# Revit family: Elite_XXXX_Standard
name_source: partatom
category: Windows
revit_build: Autodesk Revit 2014 (Build: 20130308_1515(x64)
units: mm (PartAtom-declared; Revit-internal decimal feet)

## types (42) — shared parameters
Astragal Sash Gap = 1 mm  [stored 0.00328084 ft]
Centered In Wall = Yes
Custom Sash Width Side = 800 mm  [stored 2.62467 ft]
Default Sill Height = 800 mm  [stored 2.62467 ft]
Description = Elite Slideing Window XXXX
Equal Sash Width = Yes
Frame Thickness = 70 mm
Glass Type = Glass
Glazing Thickness = 4 mm  [stored 0.0131234 ft]
Limit Sash Height Max = 1800 mm  [stored 5.90551 ft]
Limit Sash Height Min = 300 mm  [stored 0.984252 ft]
Limit Sash Width Max = 1500 mm  [stored 4.92126 ft]
Limit Sash Width Min = 300 mm  [stored 0.984252 ft]
Limit Sash Width Side Min = 300 mm  [stored 0.984252 ft]
Limit Window Height Min = 383 mm  [stored 1.25656 ft]
Limit Window Width Min = 1167 mm
Manufacturer = Crealco
Model = Elite Slideing Window XXXX
Sash Frame Seal = 1 mm  [stored 0.00328084 ft]
Sash Rail Fore Aft Spacing = 5 mm  [stored 0.0164042 ft]
Sash Side Spacing = 1 mm  [stored 0.00328084 ft]
Wall Closure = By host
zero-valued in all types: Custom Frame Offset From Exterior

## per-type parameters (varying)
| type | Area Middle Sash Glazing | Area Side Sash Glazing | Custom Windload | Custom Window Height | Custom Window Width | Height | Inside Heavy Duty Interlocker | Interlocker Configuration | Limit Sash Width Side Max | Limit Window Height Max | Limit Window Width Max | Max Pane Area | Outside Heavy Duty Interlocker | Sash Height | Sash Width Middle | Sash Width Sides | Width | Windload Design |
| XXXX_Custom | 0.23 m² | 0.23 m² | 1000 mm  [stored 3.28084 ft] | 590 mm  [stored 1.9357 ft] | 2390 mm  [stored 7.84121 ft] | 590 mm  [stored 1.9357 ft] | No | 0 mm  [stored 0 ft] | 912 mm | 1883 mm | 2990 mm  [stored 9.80971 ft] | 0.23 m² | No | 507 mm | 606 mm | 606 mm | 2390 mm  [stored 7.84121 ft] | 1000 mm  [stored 3.28084 ft] |
| Elite-2406XXXX-1000Pa | 0.23 m² | 0.23 m² | 1000 mm  [stored 3.28084 ft] | 590 mm  [stored 1.9357 ft] | 2390 mm  [stored 7.84121 ft] | 590 mm  [stored 1.9357 ft] | No | 0 mm  [stored 0 ft] | 912 mm | 1883 mm | 2990 mm  [stored 9.80971 ft] | 0.23 m² | No | 507 mm | 606 mm | 606 mm | 2390 mm  [stored 7.84121 ft] | 1000 mm  [stored 3.28084 ft] |
| Elite-2406XXXX-1500Pa | 0.23 m² | 0.23 m² | 1500 mm  [stored 4.92126 ft] | 590 mm  [stored 1.9357 ft] | 2390 mm  [stored 7.84121 ft] | 590 mm  [stored 1.9357 ft] | No | 0 mm  [stored 0 ft] | 912 mm | 1883 mm | 2990 mm  [stored 9.80971 ft] | 0.23 m² | No | 507 mm | 606 mm | 606 mm | 2390 mm  [stored 7.84121 ft] | 1500 mm  [stored 4.92126 ft] |
| Elite-2406XXXX-2000Pa | 0.23 m² | 0.23 m² | 2000 mm  [stored 6.56168 ft] | 590 mm  [stored 1.9357 ft] | 2390 mm  [stored 7.84121 ft] | 590 mm  [stored 1.9357 ft] | No | 0 mm  [stored 0 ft] | 912 mm | 1490 mm  [stored 4.88845 ft] | 2990 mm  [stored 9.80971 ft] | 0.23 m² | No | 507 mm | 606 mm | 606 mm | 2390 mm  [stored 7.84121 ft] | 2000 mm  [stored 6.56168 ft] |
| Elite-2706XXXX-1000Pa | 0.26 m² | 0.26 m² | 1000 mm  [stored 3.28084 ft] | 590 mm  [stored 1.9357 ft] | 2690 mm | 590 mm  [stored 1.9357 ft] | No | 0 mm  [stored 0 ft] | 1062 mm | 1883 mm | 2990 mm  [stored 9.80971 ft] | 0.26 m² | No | 507 mm | 681 mm | 681 mm | 2690 mm | 1000 mm  [stored 3.28084 ft] |
| Elite-2706XXXX-1500Pa | 0.26 m² | 0.26 m² | 1500 mm  [stored 4.92126 ft] | 590 mm  [stored 1.9357 ft] | 2690 mm | 590 mm  [stored 1.9357 ft] | No | 0 mm  [stored 0 ft] | 1062 mm | 1883 mm | 2990 mm  [stored 9.80971 ft] | 0.26 m² | No | 507 mm | 681 mm | 681 mm | 2690 mm | 1500 mm  [stored 4.92126 ft] |
| Elite-2706XXXX-2000Pa | 0.26 m² | 0.26 m² | 2000 mm  [stored 6.56168 ft] | 590 mm  [stored 1.9357 ft] | 2690 mm | 590 mm  [stored 1.9357 ft] | No | 0 mm  [stored 0 ft] | 1062 mm | 1490 mm  [stored 4.88845 ft] | 2990 mm  [stored 9.80971 ft] | 0.26 m² | No | 507 mm | 681 mm | 681 mm | 2690 mm | 2000 mm  [stored 6.56168 ft] |
| Elite-3006XXXX-1000Pa | 0.29 m² | 0.29 m² | 1000 mm  [stored 3.28084 ft] | 590 mm  [stored 1.9357 ft] | 2990 mm  [stored 9.80971 ft] | 590 mm  [stored 1.9357 ft] | No | 0 mm  [stored 0 ft] | 1212 mm | 1883 mm | 2990 mm  [stored 9.80971 ft] | 0.29 m² | No | 507 mm | 756 mm | 756 mm | 2990 mm  [stored 9.80971 ft] | 1000 mm  [stored 3.28084 ft] |
| Elite-3006XXXX-1500Pa | 0.29 m² | 0.29 m² | 1500 mm  [stored 4.92126 ft] | 590 mm  [stored 1.9357 ft] | 2990 mm  [stored 9.80971 ft] | 590 mm  [stored 1.9357 ft] | No | 0 mm  [stored 0 ft] | 1212 mm | 1883 mm | 2990 mm  [stored 9.80971 ft] | 0.29 m² | No | 507 mm | 756 mm | 756 mm | 2990 mm  [stored 9.80971 ft] | 1500 mm  [stored 4.92126 ft] |
| Elite-3006XXXX-2000Pa | 0.29 m² | 0.29 m² | 2000 mm  [stored 6.56168 ft] | 590 mm  [stored 1.9357 ft] | 2990 mm  [stored 9.80971 ft] | 590 mm  [stored 1.9357 ft] | No | 0 mm  [stored 0 ft] | 1212 mm | 1490 mm  [stored 4.88845 ft] | 2990 mm  [stored 9.80971 ft] | 0.29 m² | No | 507 mm | 756 mm | 756 mm | 2990 mm  [stored 9.80971 ft] | 2000 mm  [stored 6.56168 ft] |
| Elite-2409XXXX-1000Pa | 0.39 m² | 0.39 m² | 1000 mm  [stored 3.28084 ft] | 890 mm  [stored 2.91995 ft] | 2390 mm  [stored 7.84121 ft] | 890 mm  [stored 2.91995 ft] | No | 0 mm  [stored 0 ft] | 912 mm | 1883 mm | 2990 mm  [stored 9.80971 ft] | 0.39 m² | No | 807 mm  [stored 2.64764 ft] | 606 mm | 606 mm | 2390 mm  [stored 7.84121 ft] | 1000 mm  [stored 3.28084 ft] |
| Elite-2409XXXX-1500Pa | 0.39 m² | 0.39 m² | 1500 mm  [stored 4.92126 ft] | 890 mm  [stored 2.91995 ft] | 2390 mm  [stored 7.84121 ft] | 890 mm  [stored 2.91995 ft] | No | 0 mm  [stored 0 ft] | 912 mm | 1883 mm | 2990 mm  [stored 9.80971 ft] | 0.39 m² | No | 807 mm  [stored 2.64764 ft] | 606 mm | 606 mm | 2390 mm  [stored 7.84121 ft] | 1500 mm  [stored 4.92126 ft] |
| Elite-2409XXXX-2000Pa | 0.39 m² | 0.39 m² | 2000 mm  [stored 6.56168 ft] | 890 mm  [stored 2.91995 ft] | 2390 mm  [stored 7.84121 ft] | 890 mm  [stored 2.91995 ft] | No | 0 mm  [stored 0 ft] | 912 mm | 1490 mm  [stored 4.88845 ft] | 2990 mm  [stored 9.80971 ft] | 0.39 m² | No | 807 mm  [stored 2.64764 ft] | 606 mm | 606 mm | 2390 mm  [stored 7.84121 ft] | 2000 mm  [stored 6.56168 ft] |
| Elite-2709XXXX-1000Pa | 0.44 m² | 0.44 m² | 1000 mm  [stored 3.28084 ft] | 890 mm  [stored 2.91995 ft] | 2690 mm | 890 mm  [stored 2.91995 ft] | No | 0 mm  [stored 0 ft] | 1062 mm | 1883 mm | 2990 mm  [stored 9.80971 ft] | 0.44 m² | No | 807 mm  [stored 2.64764 ft] | 681 mm | 681 mm | 2690 mm | 1000 mm  [stored 3.28084 ft] |
| Elite-2709XXXX-1500Pa | 0.44 m² | 0.44 m² | 1500 mm  [stored 4.92126 ft] | 890 mm  [stored 2.91995 ft] | 2690 mm | 890 mm  [stored 2.91995 ft] | No | 0 mm  [stored 0 ft] | 1062 mm | 1883 mm | 2990 mm  [stored 9.80971 ft] | 0.44 m² | No | 807 mm  [stored 2.64764 ft] | 681 mm | 681 mm | 2690 mm | 1500 mm  [stored 4.92126 ft] |
| Elite-2709XXXX-2000Pa | 0.44 m² | 0.44 m² | 2000 mm  [stored 6.56168 ft] | 890 mm  [stored 2.91995 ft] | 2690 mm | 890 mm  [stored 2.91995 ft] | No | 0 mm  [stored 0 ft] | 1062 mm | 1490 mm  [stored 4.88845 ft] | 2990 mm  [stored 9.80971 ft] | 0.44 m² | No | 807 mm  [stored 2.64764 ft] | 681 mm | 681 mm | 2690 mm | 2000 mm  [stored 6.56168 ft] |
| Elite-3009XXXX-1000Pa | 0.5 m² | 0.5 m² | 1000 mm  [stored 3.28084 ft] | 890 mm  [stored 2.91995 ft] | 2990 mm  [stored 9.80971 ft] | 890 mm  [stored 2.91995 ft] | No | 0 mm  [stored 0 ft] | 1212 mm | 1883 mm | 2990 mm  [stored 9.80971 ft] | 0.5 m² | No | 807 mm  [stored 2.64764 ft] | 756 mm | 756 mm | 2990 mm  [stored 9.80971 ft] | 1000 mm  [stored 3.28084 ft] |
| Elite-3009XXXX-1500Pa | 0.5 m² | 0.5 m² | 1500 mm  [stored 4.92126 ft] | 890 mm  [stored 2.91995 ft] | 2990 mm  [stored 9.80971 ft] | 890 mm  [stored 2.91995 ft] | No | 0 mm  [stored 0 ft] | 1212 mm | 1883 mm | 2990 mm  [stored 9.80971 ft] | 0.5 m² | No | 807 mm  [stored 2.64764 ft] | 756 mm | 756 mm | 2990 mm  [stored 9.80971 ft] | 1500 mm  [stored 4.92126 ft] |
| Elite-3009XXXX-2000Pa | 0.5 m² | 0.5 m² | 2000 mm  [stored 6.56168 ft] | 890 mm  [stored 2.91995 ft] | 2990 mm  [stored 9.80971 ft] | 890 mm  [stored 2.91995 ft] | No | 0 mm  [stored 0 ft] | 1212 mm | 1490 mm  [stored 4.88845 ft] | 2990 mm  [stored 9.80971 ft] | 0.5 m² | No | 807 mm  [stored 2.64764 ft] | 756 mm | 756 mm | 2990 mm  [stored 9.80971 ft] | 2000 mm  [stored 6.56168 ft] |
| Elite-2412XXXX-1000Pa | 0.55 m² | 0.55 m² | 1000 mm  [stored 3.28084 ft] | 1190 mm  [stored 3.9042 ft] | 2390 mm  [stored 7.84121 ft] | 1190 mm  [stored 3.9042 ft] | No | 0 mm  [stored 0 ft] | 912 mm | 1883 mm | 2990 mm  [stored 9.80971 ft] | 0.55 m² | No | 1107 mm  [stored 3.63189 ft] | 606 mm | 606 mm | 2390 mm  [stored 7.84121 ft] | 1000 mm  [stored 3.28084 ft] |
| Elite-2412XXXX-1500Pa | 0.55 m² | 0.55 m² | 1500 mm  [stored 4.92126 ft] | 1190 mm  [stored 3.9042 ft] | 2390 mm  [stored 7.84121 ft] | 1190 mm  [stored 3.9042 ft] | No | 0 mm  [stored 0 ft] | 912 mm | 1883 mm | 2990 mm  [stored 9.80971 ft] | 0.55 m² | No | 1107 mm  [stored 3.63189 ft] | 606 mm | 606 mm | 2390 mm  [stored 7.84121 ft] | 1500 mm  [stored 4.92126 ft] |
| Elite-2412XXXX-2000Pa | 0.55 m² | 0.55 m² | 2000 mm  [stored 6.56168 ft] | 1190 mm  [stored 3.9042 ft] | 2390 mm  [stored 7.84121 ft] | 1190 mm  [stored 3.9042 ft] | Yes | 1 mm  [stored 0.00328084 ft] | 912 mm | 1490 mm  [stored 4.88845 ft] | 2990 mm  [stored 9.80971 ft] | 0.55 m² | No | 1107 mm  [stored 3.63189 ft] | 606 mm | 606 mm | 2390 mm  [stored 7.84121 ft] | 2000 mm  [stored 6.56168 ft] |
| Elite-2712XXXX-1000Pa | 0.63 m² | 0.63 m² | 1000 mm  [stored 3.28084 ft] | 1190 mm  [stored 3.9042 ft] | 2690 mm | 1190 mm  [stored 3.9042 ft] | No | 0 mm  [stored 0 ft] | 1062 mm | 1883 mm | 2990 mm  [stored 9.80971 ft] | 0.63 m² | No | 1107 mm  [stored 3.63189 ft] | 681 mm | 681 mm | 2690 mm | 1000 mm  [stored 3.28084 ft] |
| Elite-2712XXXX-1500Pa | 0.63 m² | 0.63 m² | 1500 mm  [stored 4.92126 ft] | 1190 mm  [stored 3.9042 ft] | 2690 mm | 1190 mm  [stored 3.9042 ft] | No | 0 mm  [stored 0 ft] | 1062 mm | 1883 mm | 2990 mm  [stored 9.80971 ft] | 0.63 m² | No | 1107 mm  [stored 3.63189 ft] | 681 mm | 681 mm | 2690 mm | 1500 mm  [stored 4.92126 ft] |
| Elite-2712XXXX-2000Pa | 0.63 m² | 0.63 m² | 2000 mm  [stored 6.56168 ft] | 1190 mm  [stored 3.9042 ft] | 2690 mm | 1190 mm  [stored 3.9042 ft] | Yes | 1 mm  [stored 0.00328084 ft] | 1062 mm | 1490 mm  [stored 4.88845 ft] | 2990 mm  [stored 9.80971 ft] | 0.63 m² | No | 1107 mm  [stored 3.63189 ft] | 681 mm | 681 mm | 2690 mm | 2000 mm  [stored 6.56168 ft] |
| Elite-3012XXXX-1000Pa | 0.7 m² | 0.7 m² | 1000 mm  [stored 3.28084 ft] | 1190 mm  [stored 3.9042 ft] | 2990 mm  [stored 9.80971 ft] | 1190 mm  [stored 3.9042 ft] | No | 0 mm  [stored 0 ft] | 1212 mm | 1883 mm | 2990 mm  [stored 9.80971 ft] | 0.7 m² | No | 1107 mm  [stored 3.63189 ft] | 756 mm | 756 mm | 2990 mm  [stored 9.80971 ft] | 1000 mm  [stored 3.28084 ft] |
| Elite-3012XXXX-1500Pa | 0.7 m² | 0.7 m² | 1500 mm  [stored 4.92126 ft] | 1190 mm  [stored 3.9042 ft] | 2990 mm  [stored 9.80971 ft] | 1190 mm  [stored 3.9042 ft] | Yes | 1 mm  [stored 0.00328084 ft] | 1212 mm | 1883 mm | 2990 mm  [stored 9.80971 ft] | 0.7 m² | No | 1107 mm  [stored 3.63189 ft] | 756 mm | 756 mm | 2990 mm  [stored 9.80971 ft] | 1500 mm  [stored 4.92126 ft] |
| Elite-3012XXXX-2000Pa | 0.7 m² | 0.7 m² | 2000 mm  [stored 6.56168 ft] | 1190 mm  [stored 3.9042 ft] | 2990 mm  [stored 9.80971 ft] | 1190 mm  [stored 3.9042 ft] | Yes | 1 mm  [stored 0.00328084 ft] | 1212 mm | 1490 mm  [stored 4.88845 ft] | 2990 mm  [stored 9.80971 ft] | 0.7 m² | No | 1107 mm  [stored 3.63189 ft] | 756 mm | 756 mm | 2990 mm  [stored 9.80971 ft] | 2000 mm  [stored 6.56168 ft] |
| Elite-2415XXXX-1000Pa | 0.72 m² | 0.72 m² | 1000 mm  [stored 3.28084 ft] | 1490 mm  [stored 4.88845 ft] | 2390 mm  [stored 7.84121 ft] | 1490 mm  [stored 4.88845 ft] | Yes | 1 mm  [stored 0.00328084 ft] | 912 mm | 1883 mm | 2990 mm  [stored 9.80971 ft] | 0.72 m² | No | 1407 mm  [stored 4.61614 ft] | 606 mm | 606 mm | 2390 mm  [stored 7.84121 ft] | 1000 mm  [stored 3.28084 ft] |
| Elite-2415XXXX-1500Pa | 0.72 m² | 0.72 m² | 1500 mm  [stored 4.92126 ft] | 1490 mm  [stored 4.88845 ft] | 2390 mm  [stored 7.84121 ft] | 1490 mm  [stored 4.88845 ft] | Yes | 1 mm  [stored 0.00328084 ft] | 912 mm | 1883 mm | 2990 mm  [stored 9.80971 ft] | 0.72 m² | No | 1407 mm  [stored 4.61614 ft] | 606 mm | 606 mm | 2390 mm  [stored 7.84121 ft] | 1500 mm  [stored 4.92126 ft] |
| Elite-2415XXXX-2000Pa | 0.72 m² | 0.72 m² | 2000 mm  [stored 6.56168 ft] | 1490 mm  [stored 4.88845 ft] | 2390 mm  [stored 7.84121 ft] | 1490 mm  [stored 4.88845 ft] | Yes | 1 mm  [stored 0.00328084 ft] | 912 mm | 1490 mm  [stored 4.88845 ft] | 2990 mm  [stored 9.80971 ft] | 0.72 m² | No | 1407 mm  [stored 4.61614 ft] | 606 mm | 606 mm | 2390 mm  [stored 7.84121 ft] | 2000 mm  [stored 6.56168 ft] |
| Elite-2715XXXX-1000Pa | 0.81 m² | 0.81 m² | 1000 mm  [stored 3.28084 ft] | 1490 mm  [stored 4.88845 ft] | 2690 mm | 1490 mm  [stored 4.88845 ft] | Yes | 1 mm  [stored 0.00328084 ft] | 1062 mm | 1883 mm | 2990 mm  [stored 9.80971 ft] | 0.81 m² | No | 1407 mm  [stored 4.61614 ft] | 681 mm | 681 mm | 2690 mm | 1000 mm  [stored 3.28084 ft] |
| Elite-2715XXXX-1500Pa | 0.81 m² | 0.81 m² | 1500 mm  [stored 4.92126 ft] | 1490 mm  [stored 4.88845 ft] | 2690 mm | 1490 mm  [stored 4.88845 ft] | Yes | 1 mm  [stored 0.00328084 ft] | 1062 mm | 1883 mm | 2990 mm  [stored 9.80971 ft] | 0.81 m² | No | 1407 mm  [stored 4.61614 ft] | 681 mm | 681 mm | 2690 mm | 1500 mm  [stored 4.92126 ft] |
| Elite-2715XXXX-2000Pa | 0.81 m² | 0.81 m² | 2000 mm  [stored 6.56168 ft] | 1490 mm  [stored 4.88845 ft] | 2690 mm | 1490 mm  [stored 4.88845 ft] | Yes | 2 mm  [stored 0.00656168 ft] | 1062 mm | 1490 mm  [stored 4.88845 ft] | 2990 mm  [stored 9.80971 ft] | 0.81 m² | Yes | 1407 mm  [stored 4.61614 ft] | 681 mm | 681 mm | 2690 mm | 2000 mm  [stored 6.56168 ft] |
| Elite-3015XXXX-1000Pa | 0.91 m² | 0.91 m² | 1000 mm  [stored 3.28084 ft] | 1490 mm  [stored 4.88845 ft] | 2990 mm  [stored 9.80971 ft] | 1490 mm  [stored 4.88845 ft] | Yes | 1 mm  [stored 0.00328084 ft] | 1212 mm | 1883 mm | 2990 mm  [stored 9.80971 ft] | 0.91 m² | No | 1407 mm  [stored 4.61614 ft] | 756 mm | 756 mm | 2990 mm  [stored 9.80971 ft] | 1000 mm  [stored 3.28084 ft] |
| Elite-3015XXXX-1500Pa | 0.91 m² | 0.91 m² | 1500 mm  [stored 4.92126 ft] | 1490 mm  [stored 4.88845 ft] | 2990 mm  [stored 9.80971 ft] | 1490 mm  [stored 4.88845 ft] | Yes | 1 mm  [stored 0.00328084 ft] | 1212 mm | 1883 mm | 2990 mm  [stored 9.80971 ft] | 0.91 m² | No | 1407 mm  [stored 4.61614 ft] | 756 mm | 756 mm | 2990 mm  [stored 9.80971 ft] | 1500 mm  [stored 4.92126 ft] |
| Elite-3015XXXX-2000Pa | 0.91 m² | 0.91 m² | 2000 mm  [stored 6.56168 ft] | 1490 mm  [stored 4.88845 ft] | 2990 mm  [stored 9.80971 ft] | 1490 mm  [stored 4.88845 ft] | Yes | 2 mm  [stored 0.00656168 ft] | 1212 mm | 1490 mm  [stored 4.88845 ft] | 2990 mm  [stored 9.80971 ft] | 0.91 m² | Yes | 1407 mm  [stored 4.61614 ft] | 756 mm | 756 mm | 2990 mm  [stored 9.80971 ft] | 2000 mm  [stored 6.56168 ft] |
| Elite-2418XXXX-1000Pa | 0.88 m² | 0.88 m² | 1000 mm  [stored 3.28084 ft] | 1790 mm  [stored 5.8727 ft] | 2390 mm  [stored 7.84121 ft] | 1790 mm  [stored 5.8727 ft] | Yes | 1 mm  [stored 0.00328084 ft] | 912 mm | 1883 mm | 2990 mm  [stored 9.80971 ft] | 0.88 m² | No | 1707 mm | 606 mm | 606 mm | 2390 mm  [stored 7.84121 ft] | 1000 mm  [stored 3.28084 ft] |
| Elite-2418XXXX-1500Pa | 0.88 m² | 0.88 m² | 1500 mm  [stored 4.92126 ft] | 1790 mm  [stored 5.8727 ft] | 2390 mm  [stored 7.84121 ft] | 1790 mm  [stored 5.8727 ft] | Yes | 2 mm  [stored 0.00656168 ft] | 912 mm | 1883 mm | 2690 mm | 0.88 m² | Yes | 1707 mm | 606 mm | 606 mm | 2390 mm  [stored 7.84121 ft] | 1500 mm  [stored 4.92126 ft] |
| Elite-2718XXXX-1000Pa | 1 m² | 1 m² | 1000 mm  [stored 3.28084 ft] | 1790 mm  [stored 5.8727 ft] | 2690 mm | 1790 mm  [stored 5.8727 ft] | Yes | 2 mm  [stored 0.00656168 ft] | 1062 mm | 1883 mm | 2990 mm  [stored 9.80971 ft] | 1 m² | Yes | 1707 mm | 681 mm | 681 mm | 2690 mm | 1000 mm  [stored 3.28084 ft] |
| Elite-2718XXXX-1500Pa | 1 m² | 1 m² | 1500 mm  [stored 4.92126 ft] | 1790 mm  [stored 5.8727 ft] | 2690 mm | 1790 mm  [stored 5.8727 ft] | Yes | 2 mm  [stored 0.00656168 ft] | 1062 mm | 1883 mm | 2690 mm | 1 m² | Yes | 1707 mm | 681 mm | 681 mm | 2690 mm | 1500 mm  [stored 4.92126 ft] |
| Elite-3018XXXX-1000Pa | 1.12 m² | 1.12 m² | 1000 mm  [stored 3.28084 ft] | 1790 mm  [stored 5.8727 ft] | 2990 mm  [stored 9.80971 ft] | 1790 mm  [stored 5.8727 ft] | Yes | 2 mm  [stored 0.00656168 ft] | 1212 mm | 1883 mm | 2990 mm  [stored 9.80971 ft] | 1.12 m² | Yes | 1707 mm | 756 mm | 756 mm | 2990 mm  [stored 9.80971 ft] | 1000 mm  [stored 3.28084 ft] |

note: [stored X ft] marks values corroborated as IEEE doubles in the binary element streams (Revit-internal decimal feet)

## geometry (parser evidence)
native form markers: Sweep x45
no freeform markers — native parametric forms only
